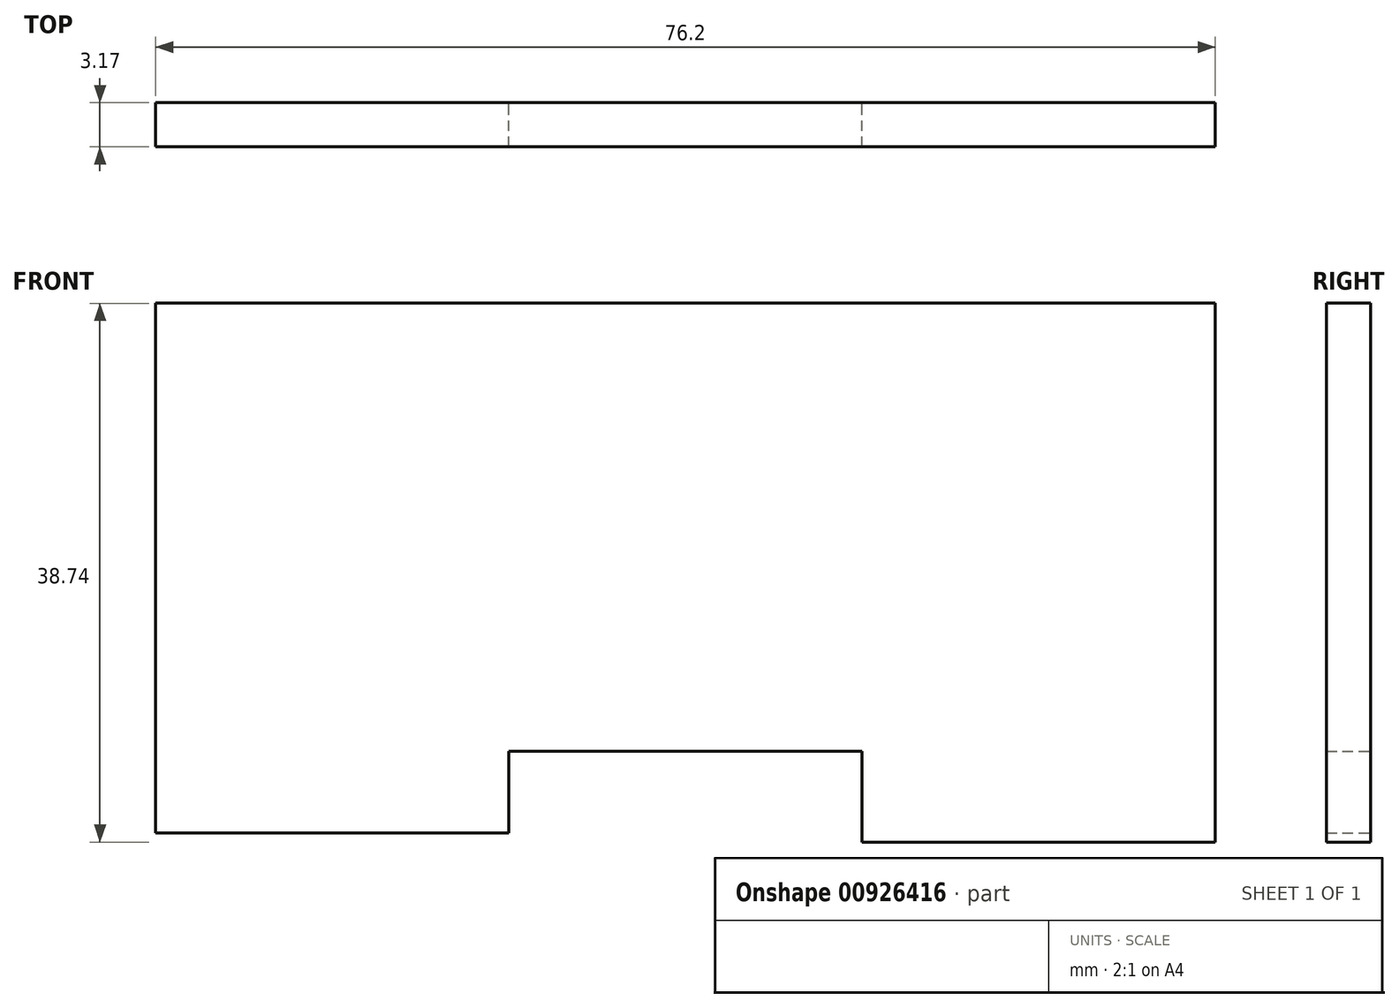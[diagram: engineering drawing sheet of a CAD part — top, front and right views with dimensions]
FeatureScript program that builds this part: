
annotation { "Feature Type Name" : "Feature", "Feature Type Description" : "" }
export const myFeature = defineFeature(function(context is Context, id is Id, definition is map)
    precondition{}
    {
        {
            var Q0;
            Q0=qCreatedBy(makeId("Front.planeOp"),FACE);
            var sketch = newSketch(context, id + "F0", { "sketchPlane" : qUnion([Q0])});
            skLineSegment(sketch, "E0", {"start": v(-35.83, -12.52) * mm, "end": v(-10.43, -12.52) * mm});
            skLineSegment(sketch, "E1", {"start": v(-10.43, -12.52) * mm, "end": v(-10.43, -6.64) * mm});
            skLineSegment(sketch, "E2", {"start": v(-10.43, -6.64) * mm, "end": v(14.97, -6.64) * mm});
            skLineSegment(sketch, "E3", {"start": v(14.97, -6.64) * mm, "end": v(14.97, -13.16) * mm});
            skLineSegment(sketch, "E4", {"start": v(14.97, -13.16) * mm, "end": v(40.37, -13.16) * mm});
            skLineSegment(sketch, "E5", {"start": v(40.37, -13.16) * mm, "end": v(40.37, 25.58) * mm});
            skLineSegment(sketch, "E6", {"start": v(40.37, 25.58) * mm, "end": v(-35.83, 25.58) * mm});
            skLineSegment(sketch, "E7", {"start": v(-35.83, 25.58) * mm, "end": v(-35.83, -12.52) * mm});
            skSolve(sketch);
        }
        {
            var Q0;
            Q0 = qSketchRegion(id + "F0", true);
            extrude(context, id + "F1", {"entities" : qUnion([Q0]), "depth" : 3.17 * mm, "offsetDistance" : 25.4 * mm});
        }
    });
